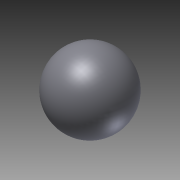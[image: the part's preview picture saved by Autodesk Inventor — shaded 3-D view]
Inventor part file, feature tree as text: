
AUTODESK INVENTOR PART (.ipt)
format: ipt  version: 2012 SP1 (Build 160190100, 190)  size: 101,376 bytes
history: native  units: in
note: dims shown in document units (in); Inventor stores cm internally (conversion verified against a paired STEP export)
features: revolve x1, sketch x1
ambient origin geometry x8: Origin, YZ Plane, XZ Plane, XY Plane, X Axis, Y Axis, Z Axis, Center Point
bodies: Solid1 (feature_tree)
feature tree (2):
  revolve  "Revolution1"  Angle=90.0deg
  sketch  "Sketch1"  dims[d0=0.1094in d1=90.0deg]
